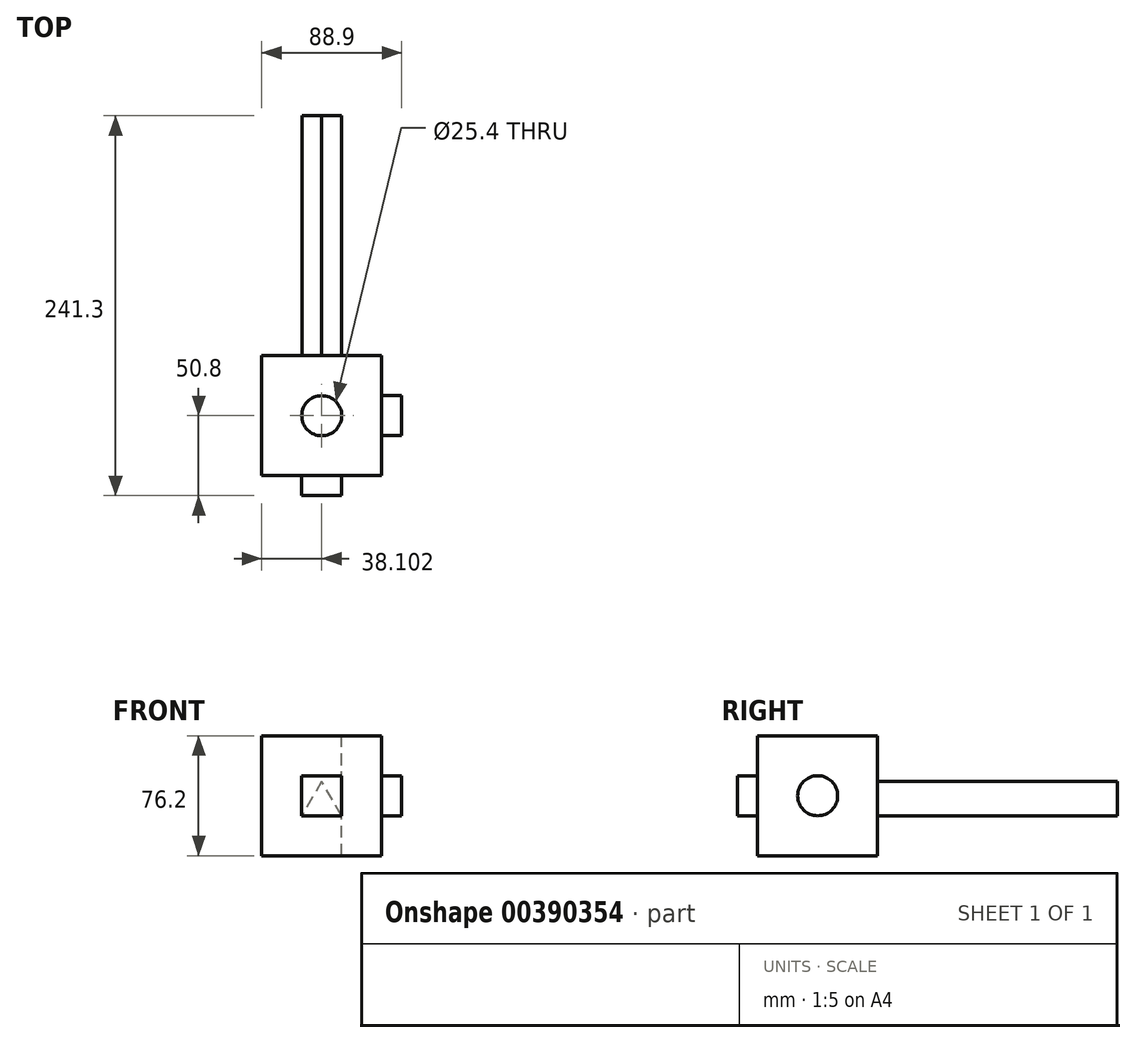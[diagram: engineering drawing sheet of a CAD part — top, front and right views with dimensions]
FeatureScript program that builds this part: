
annotation { "Feature Type Name" : "Feature", "Feature Type Description" : "" }
export const myFeature = defineFeature(function(context is Context, id is Id, definition is map)
    precondition{}
    {
        {
            var Q0;
            Q0=qCreatedBy(makeId("Front.planeOp"),FACE);
            var sketch = newSketch(context, id + "F0", { "sketchPlane" : qUnion([Q0])});
            skLineSegment(sketch, "E0.bottom", {"start": v(-45.55, -22.34) * mm, "end": v(30.65, -22.34) * mm});
            skLineSegment(sketch, "E0.top", {"start": v(-45.55, 53.86) * mm, "end": v(30.65, 53.86) * mm});
            skLineSegment(sketch, "E0.left", {"start": v(-45.55, -22.34) * mm, "end": v(-45.55, 53.86) * mm});
            skLineSegment(sketch, "E0.right", {"start": v(30.65, -22.34) * mm, "end": v(30.65, 53.86) * mm});
            skSolve(sketch);
        }
        {
            var Q0;
            Q0=makeQuery(id+"F0.imprint","IMPRINT",FACE,{"disambiguationData":[TD([[makeQuery(id+"F0.imprint","IMPRINT",EDGE,{"derivedFrom":sQuery(id+"F0.wireOp",EDGE,"E0.bottom")}),1.0]])]});
            extrude(context, id + "F1", {"entities" : qUnion([Q0]), "depth" : 76.2 * mm});
        }
        {
            var Q0;
            Q0=makeQuery(id+"F1.opExtrude","SWEPT_FACE",FACE,{"disambiguationData":[OSD([sQuery(id+"F0.wireOp",EDGE,"E0.top")])]});
            var sketch = newSketch(context, id + "F2", { "sketchPlane" : qUnion([Q0])});
            skPoint(sketch, "E1", {"position": v(-7.45, -38.1) * mm});
            skSolve(sketch);
        }
        {
            var Q0;
            Q0=sQuery(id+"F2.wireOp",VERTEX,"E1");
            var Q1;
            Q1=makeQuery(id+"F1.opExtrude","SWEPT_BODY",BODY,{"disambiguationData":[OSD([sQuery(id+"F0.wireOp",EDGE,"E0.bottom"),sQuery(id+"F0.wireOp",EDGE,"E0.top"),sQuery(id+"F0.wireOp",EDGE,"E0.left"),sQuery(id+"F0.wireOp",EDGE,"E0.right")])]});
            hole(context, id + "F3", {"style" : HoleStyle.SIMPLE, "endStyle" : HoleEndStyle.THROUGH, "holeDiameter" : 25.4 * mm, "isTappedThrough" : true, "tappedDepth" : 12.7 * mm, "tapClearance" : 3, "locations" : qUnion([Q0]), "scope" : qUnion([Q1])});
        }
        {
            var Q0;
            Q0=makeQuery(id+"F1.opExtrude","CAP_FACE",FACE,{"disambiguationData":[OSD([sQuery(id+"F0.wireOp",EDGE,"E0.bottom"),sQuery(id+"F0.wireOp",EDGE,"E0.top"),sQuery(id+"F0.wireOp",EDGE,"E0.left"),sQuery(id+"F0.wireOp",EDGE,"E0.right")])],"isStart":false});
            var sketch = newSketch(context, id + "F4", { "sketchPlane" : qUnion([Q0])});
            skLineSegment(sketch, "E2.bottom", {"start": v(-20.15, 28.46) * mm, "end": v(5.25, 28.46) * mm});
            skLineSegment(sketch, "E2.top", {"start": v(-20.15, 3.06) * mm, "end": v(5.25, 3.06) * mm});
            skLineSegment(sketch, "E2.left", {"start": v(-20.15, 28.46) * mm, "end": v(-20.15, 3.06) * mm});
            skLineSegment(sketch, "E2.right", {"start": v(5.25, 28.46) * mm, "end": v(5.25, 3.06) * mm});
            skSolve(sketch);
        }
        {
            var Q0;
            Q0=makeQuery(id+"F4.imprint","IMPRINT",FACE,{"disambiguationData":[TD([[makeQuery(id+"F4.imprint","IMPRINT",EDGE,{"derivedFrom":sQuery(id+"F4.wireOp",EDGE,"E2.bottom")}),-1.0]])]});
            extrude(context, id + "F5", {"entities" : qUnion([Q0]), "operationType" : NewBodyOperationType.ADD, "depth" : 12.7 * mm});
        }
        {
            var Q0;
            Q0=makeQuery(id+"F1.opExtrude","SWEPT_FACE",FACE,{"disambiguationData":[OSD([sQuery(id+"F0.wireOp",EDGE,"E0.right")])]});
            var sketch = newSketch(context, id + "F6", { "sketchPlane" : qUnion([Q0])});
            skCircle(sketch, "E3", {"center": v(-38.1, 15.76) * mm, "radius": 12.7 * mm});
            skSolve(sketch);
        }
        {
            var Q0;
            Q0=makeQuery(id+"F6.imprint","IMPRINT",FACE,{"disambiguationData":[TD([[makeQuery(id+"F6.imprint","IMPRINT",EDGE,{"derivedFrom":sQuery(id+"F6.wireOp",EDGE,"E3")}),1.0]])]});
            extrude(context, id + "F7", {"entities" : qUnion([Q0]), "operationType" : NewBodyOperationType.ADD, "depth" : 12.7 * mm});
        }
        {
            var Q0;
            Q0=makeQuery(id+"F1.opExtrude","CAP_FACE",FACE,{"disambiguationData":[OSD([sQuery(id+"F0.wireOp",EDGE,"E0.bottom"),sQuery(id+"F0.wireOp",EDGE,"E0.top"),sQuery(id+"F0.wireOp",EDGE,"E0.left"),sQuery(id+"F0.wireOp",EDGE,"E0.right")])],"isStart":true});
            var sketch = newSketch(context, id + "F8", { "sketchPlane" : qUnion([Q0])});
            skCircle(sketch, "E4.cCircle", {"center": v(7.45, 10.34) * mm, "radius": 7.28 * mm, "construction": true});
            skLineSegment(sketch, "E4.0", {"start": v(20.06, 3.06) * mm, "end": v(-5.17, 3.06) * mm});
            skLineSegment(sketch, "E4.1", {"start": v(-5.17, 3.06) * mm, "end": v(7.45, 24.9) * mm});
            skLineSegment(sketch, "E4.2", {"start": v(7.45, 24.9) * mm, "end": v(20.06, 3.06) * mm});
            skPoint(sketch, "E4.0.midPoint", {"position": v(7.45, 3.06) * mm});
            skSolve(sketch);
        }
        {
            var Q0;
            Q0=makeQuery(id+"F8.imprint","IMPRINT",FACE,{"disambiguationData":[TD([[makeQuery(id+"F8.imprint","IMPRINT",EDGE,{"derivedFrom":sQuery(id+"F8.wireOp",EDGE,"E4.0")}),-1.0]])]});
            extrude(context, id + "F9", {"entities" : qUnion([Q0]), "operationType" : NewBodyOperationType.ADD, "depth" : 152.4 * mm});
        }
    });
